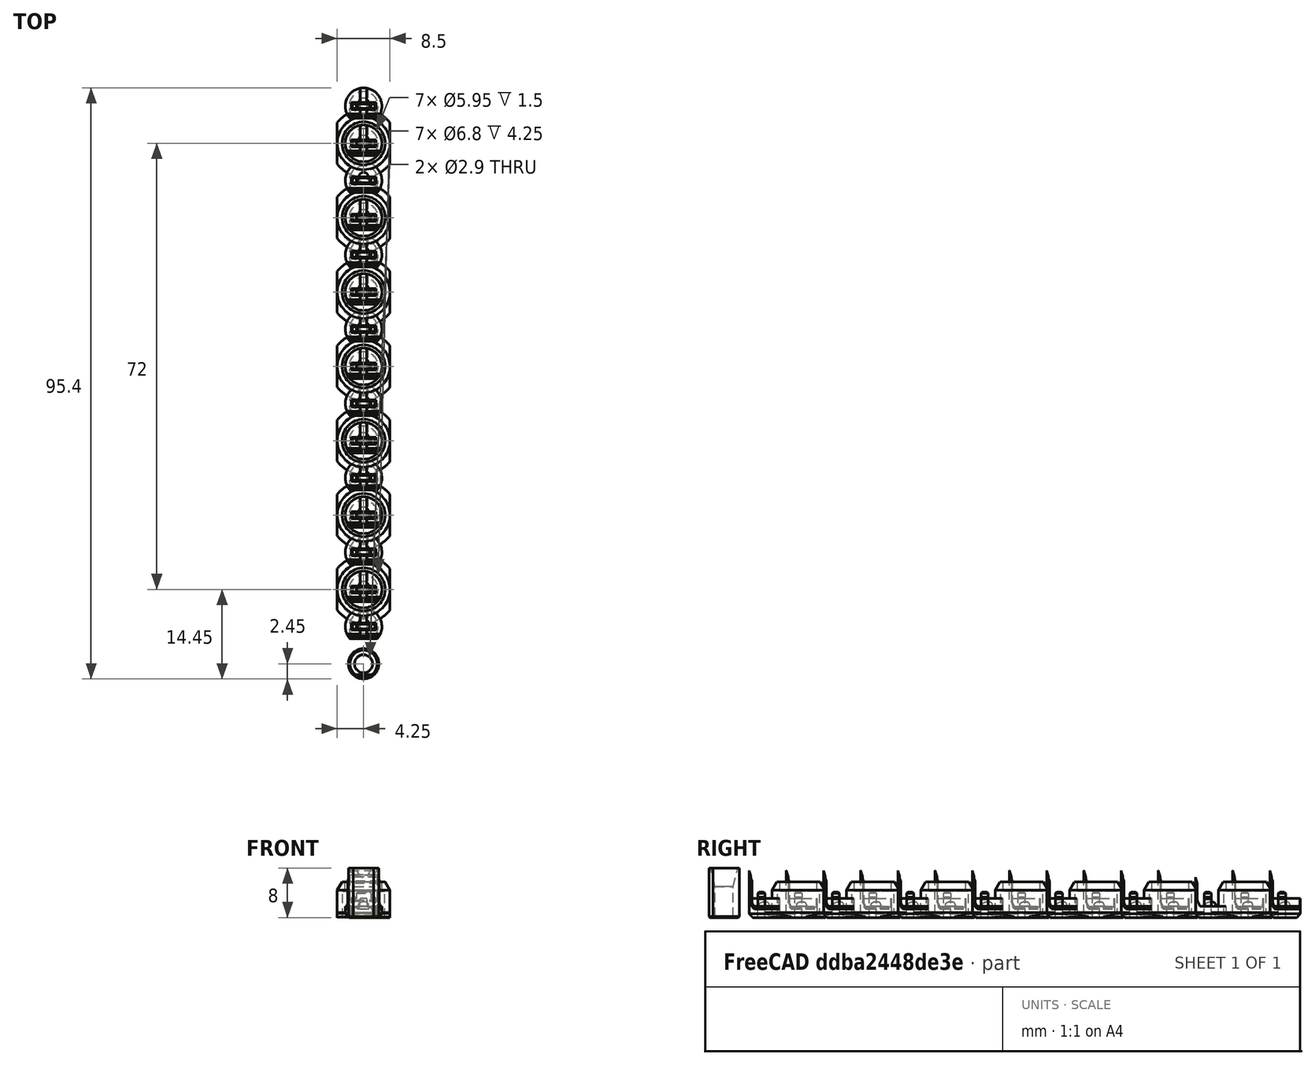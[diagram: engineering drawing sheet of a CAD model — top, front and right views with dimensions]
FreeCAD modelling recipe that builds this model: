
FCSTD DOCUMENT  (FreeCAD 0.21R33771 (Git))
Label: universal_insert
License: All rights reserved
LicenseURL: http://en.wikipedia.org/wiki/All_rights_reserved
objects: PartDesign::Body×90, PartDesign::FeatureBase×82, Sketcher::SketchObject×19, PartDesign::Pad×9, PartDesign::Pocket×7, PartDesign::Chamfer×7, App::Part×6, PartDesign::Revolution×3, PartDesign::Fillet×2, PartDesign::Draft×1
note: 249 computed .brp shape members not serialized (recipe doc carries the construction recipe); baked Part::Feature solids carry a one-line shape summary decoded from their .brp

FEATURE [Sketcher::SketchObject] Sketch
  FullyConstrained = false
  MapMode = 5
  Support = -> [XY_Plane]
  sketch-geometry (2):
    g0: ArcOfCircle CenterX=0 CenterY=0 CenterZ=0 NormalX=0 NormalY=0 NormalZ=1 AngleXU=0 Radius=2.95 StartAngle=5.55407 EndAngle=10.1539
    g1: LineSegment StartX=-2.2 StartY=-1.96532 StartZ=0 EndX=2.2 EndY=-1.96532 EndZ=0
  constraints (6):
    c: Coincident(g0,g-1)
    c: Coincident(g1,g0)
    c: Coincident(g1,g0)
    c: Radius(g0) = 2.95
    c: DistanceX(g1,g1) = 4.4
    c: Horizontal(g1)
FEATURE [PartDesign::Pad] Pad  label="Riser"
  AllowMultiFace = false
  Direction = (1,1,1)
  Length = 1.6
  Length2 = 100
  Profile = -> Sketch
  Refine = true
  Type = 0
FEATURE [Sketcher::SketchObject] Sketch001
  ExternalGeometry = -> [Pad]
  FullyConstrained = true
  MapMode = 5
  Placement = pos=(0,0,1.6) rot=(0,0,1;0rad)
  Support = -> [Pad]
  sketch-geometry (4):
    g0: LineSegment StartX=-0.5 StartY=-1.96532 StartZ=0 EndX=-0.5 EndY=2.90732 EndZ=0
    g1: LineSegment StartX=0.5 StartY=2.90732 StartZ=0 EndX=0.5 EndY=-1.96532 EndZ=0
    g2: ArcOfCircle CenterX=0 CenterY=0 CenterZ=0 NormalX=0 NormalY=0 NormalZ=1 AngleXU=0 Radius=2.95 StartAngle=1.40048 EndAngle=1.74111
    g3: LineSegment StartX=-0.5 StartY=-1.96532 StartZ=0 EndX=0.5 EndY=-1.96532 EndZ=0
  constraints (12):
    c: PointOnObject(g0,g-4)
    c: PointOnObject(g0,g-3)
    c: Vertical(g0)
    c: PointOnObject(g1,g-4)
    c: Vertical(g1)
    c: Coincident(g2,g-1)
    c: Coincident(g2,g0)
    c: Coincident(g2,g1)
    c: Equal(g1,g0)
    c: Coincident(g3,g0)
    c: Coincident(g3,g1)
    c: DistanceX(g3,g3) = 1
FEATURE [Sketcher::SketchObject] Sketch002
  ExternalGeometry = -> [Pad]
  FullyConstrained = false
  MapMode = 5
  Placement = pos=(0,0,1.6) rot=(0,0,1;0rad)
  Support = -> [Pad]
  sketch-geometry (4):
    g0: LineSegment StartX=-2.2 StartY=-1.96532 StartZ=0 EndX=2.2 EndY=-1.96532 EndZ=0
    g1: LineSegment StartX=-2.68803 StartY=-1.21532 StartZ=0 EndX=2.68803 EndY=-1.21532 EndZ=0
    g2: ArcOfCircle CenterX=0 CenterY=0 CenterZ=0 NormalX=0 NormalY=0 NormalZ=1 AngleXU=0 Radius=2.95 StartAngle=3.56621 EndAngle=3.87071
    g3: ArcOfCircle CenterX=0 CenterY=0 CenterZ=0 NormalX=0 NormalY=0 NormalZ=1 AngleXU=0 Radius=2.95 StartAngle=5.55407 EndAngle=5.85857
  constraints (10):
    c: Horizontal(g1)
    c: Coincident(g2,g-1)
    c: Coincident(g2,g0)
    c: Coincident(g2,g1)
    c: Coincident(g3,g2)
    c: Coincident(g3,g1)
    c: Coincident(g3,g0)
    c: DistanceY(g0,g1) = 0.75
    c: Coincident(g0,g-3)
    c: Coincident(g0,g-3)
FEATURE [PartDesign::Pad] Pad001
  AllowMultiFace = false
  BaseFeature = -> Pad
  Direction = (1,1,1)
  Length = 6
  Length2 = 100
  Profile = -> Sketch002
  Refine = true
  Type = 0
FEATURE [Sketcher::SketchObject] Sketch003
  ExternalGeometry = -> [Pad001]
  FullyConstrained = true
  MapMode = 5
  Placement = pos=(0,0,0) rot=(0.57735,0.57735,0.57735;2.0944rad)
  Support = -> [YZ_Plane]
  sketch-geometry (5):
    g0: LineSegment StartX=-1.21532 StartY=1.6 StartZ=0 EndX=-1.21532 EndY=7.6 EndZ=0
    g1: LineSegment StartX=-1.21532 StartY=1.6 StartZ=0 EndX=-1.66532 EndY=2.6 EndZ=0
    g2: LineSegment StartX=-1.96532 StartY=7.6 StartZ=0 EndX=-1.21532 EndY=7.6 EndZ=0
    g3: LineSegment StartX=-1.66532 StartY=2.6 StartZ=0 EndX=-1.66532 EndY=6.6 EndZ=0
    g4: LineSegment StartX=-1.66532 StartY=6.6 StartZ=0 EndX=-1.96532 EndY=7.6 EndZ=0
  constraints (13):
    c: Coincident(g0,g-3)
    c: Coincident(g0,g-3)
    c: Coincident(g1,g0)
    c: Horizontal(g2)
    c: Coincident(g2,g0)
    c: DistanceY(g0,g1) = 1
    c: Coincident(g3,g1)
    c: Vertical(g3)
    c: Coincident(g4,g3)
    c: Coincident(g4,g2)
    c: DistanceX(g2,g2) = 0.75
    c: DistanceY(g3,g0) = 1
    c: DistanceX(g2,g3) = 0.3
FEATURE [PartDesign::Pocket] Pocket
  AllowMultiFace = false
  BaseFeature = -> Pad001
  Direction = (1,1,1)
  Length = 5
  Length2 = 100
  Midplane = true
  Profile = -> Sketch003
  Refine = true
  Type = 1
FEATURE [PartDesign::Pad] Pad002
  AllowMultiFace = false
  BaseFeature = -> Pocket
  Direction = (1,1,1)
  Length = 1.5
  Length2 = 100
  Profile = -> Sketch001
  Refine = true
  Type = 0
FEATURE [PartDesign::Draft] Draft
  Angle = 6
  Base = -> Pad002 [Face9,Face11]
  BaseFeature = -> Pad002
  NeutralPlane = -> Pad002 [Face10]
  Reversed = true
  SupportTransform = false
FEATURE [PartDesign::Chamfer] Chamfer
  Angle = 45
  Base = -> Draft [Edge1,Edge2]
  BaseFeature = -> Draft
  ChamferType = 0
  FlipDirection = false
  Size = 0.6
  Size2 = 1
  SupportTransform = false
  UseAllEdges = false
FEATURE [PartDesign::Body] Body  label="Potentiometer"
  Group = -> [Sketch,Pad,Sketch001,Sketch002,Pad001,Sketch003,Pocket,Pad002,Draft,Chamfer]
  Origin = -> Origin
  Tip = -> Chamfer
FEATURE [Sketcher::SketchObject] Sketch004
  FullyConstrained = false
  MapMode = 5
  Support = -> [XY_Plane001]
  sketch-geometry (2):
    g0: ArcOfCircle CenterX=0 CenterY=0 CenterZ=0 NormalX=0 NormalY=0 NormalZ=1 AngleXU=0 Radius=2.95 StartAngle=5.55407 EndAngle=10.1539
    g1: LineSegment StartX=-2.2 StartY=-1.96532 StartZ=0 EndX=2.2 EndY=-1.96532 EndZ=0
  constraints (6):
    c: Coincident(g0,g-1)
    c: Coincident(g1,g0)
    c: Coincident(g1,g0)
    c: Radius(g0) = 2.95
    c: DistanceX(g1,g1) = 4.4
    c: Horizontal(g1)
FEATURE [PartDesign::Pad] Pad003  label="Riser001"
  AllowMultiFace = false
  Direction = (1,1,1)
  Length = 6.5
  Length2 = 100
  Profile = -> Sketch004
  Refine = true
  Type = 0
FEATURE [Sketcher::SketchObject] Sketch008
  FullyConstrained = true
  MapMode = 5
  Support = -> [XY_Plane002]
  sketch-geometry (7):
    g0: LineSegment StartX=-2 StartY=0.575 StartZ=0 EndX=2 EndY=0.575 EndZ=0
    g1: LineSegment StartX=2 StartY=0.575 StartZ=0 EndX=2 EndY=-0.575 EndZ=0
    g2: LineSegment StartX=2 StartY=-0.575 StartZ=0 EndX=-2 EndY=-0.575 EndZ=0
    g3: LineSegment StartX=-2 StartY=-0.575 StartZ=0 EndX=-2 EndY=0.575 EndZ=0
    g4: LineSegment StartX=-2 StartY=0.575 StartZ=0 EndX=0 EndY=0 EndZ=0
    g5: LineSegment StartX=0 StartY=0 StartZ=0 EndX=2 EndY=0.575 EndZ=0
    g6: LineSegment StartX=0 StartY=0 StartZ=0 EndX=-2 EndY=-0.575 EndZ=0
  constraints (18):
    c: Coincident(g0,g1)
    c: Coincident(g1,g2)
    c: Coincident(g2,g3)
    c: Coincident(g3,g0)
    c: Horizontal(g0)
    c: Horizontal(g2)
    c: Vertical(g1)
    c: Vertical(g3)
    c: Coincident(g4,g0)
    c: Coincident(g4,g-1)
    c: Coincident(g5,g-1)
    c: Coincident(g5,g0)
    c: Coincident(g6,g-1)
    c: Coincident(g6,g2)
    c: Equal(g6,g4)
    c: Equal(g4,g5)
    c: DistanceX(g0,g0) = 4
    c: DistanceY(g1,g1) = 1.15
FEATURE [PartDesign::Pad] Pad005  label="Riser002"
  AllowMultiFace = false
  Direction = (1,1,1)
  Length = 4.1
  Length2 = 100
  Profile = -> Sketch008
  Refine = true
  Type = 0
FEATURE [Sketcher::SketchObject] Sketch009
  ExternalGeometry = -> [Pad005]
  FullyConstrained = true
  MapMode = 5
  Placement = pos=(0,0.575,0) rot=(0,0.707107,0.707107;3.14159rad)
  Support = -> [Pad005]
  sketch-geometry (8):
    g0: LineSegment StartX=-2 StartY=4.1 StartZ=0 EndX=-1.175 EndY=4.1 EndZ=0
    g1: LineSegment StartX=-1.175 StartY=4.1 StartZ=0 EndX=-1.175 EndY=3.25 EndZ=0
    g2: LineSegment StartX=-1.175 StartY=3.25 StartZ=0 EndX=-2 EndY=3.25 EndZ=0
    g3: LineSegment StartX=-2 StartY=3.25 StartZ=0 EndX=-2 EndY=4.1 EndZ=0
    g4: LineSegment StartX=2 StartY=4.1 StartZ=0 EndX=1.175 EndY=4.1 EndZ=0
    g5: LineSegment StartX=1.175 StartY=4.1 StartZ=0 EndX=1.175 EndY=3.25 EndZ=0
    g6: LineSegment StartX=1.175 StartY=3.25 StartZ=0 EndX=2 EndY=3.25 EndZ=0
    g7: LineSegment StartX=2 StartY=3.25 StartZ=0 EndX=2 EndY=4.1 EndZ=0
  constraints (22):
    c: Coincident(g0,g1)
    c: Coincident(g1,g2)
    c: Coincident(g2,g3)
    c: Coincident(g3,g0)
    c: Horizontal(g0)
    c: Horizontal(g2)
    c: Vertical(g1)
    c: Vertical(g3)
    c: Coincident(g0,g-4)
    c: Coincident(g4,g5)
    c: Coincident(g5,g6)
    c: Coincident(g6,g7)
    c: Coincident(g7,g4)
    c: Horizontal(g4)
    c: Horizontal(g6)
    c: Vertical(g5)
    c: Vertical(g7)
    c: Coincident(g4,g-5)
    c: Equal(g4,g0)
    c: Equal(g1,g5)
    c: DistanceX(g0,g4) = 2.35
    c: DistanceY(g1,g1) = 0.85
FEATURE [PartDesign::Pocket] Pocket002
  AllowMultiFace = false
  BaseFeature = -> Pad005
  Direction = (1,1,1)
  Length = 5
  Length2 = 100
  Profile = -> Sketch009
  Refine = true
  Type = 0
FEATURE [Sketcher::SketchObject] Sketch010
  FullyConstrained = false
  MapMode = 5
  Placement = pos=(0,0,0) rot=(1,0,0;1.5708rad)
  Support = -> [XZ_Plane003]
  sketch-geometry (5):
    g0: LineSegment StartX=-1.45 StartY=0 StartZ=0 EndX=-1.45 EndY=5 EndZ=0
    g1: LineSegment StartX=-1.45 StartY=0 StartZ=0 EndX=-2.45 EndY=0 EndZ=0
    g2: LineSegment StartX=-2.45 StartY=0 StartZ=0 EndX=-2.45 EndY=8 EndZ=0
    g3: LineSegment StartX=-1.45 StartY=5 StartZ=0 EndX=-2.2 EndY=8 EndZ=0
    g4: LineSegment StartX=-2.45 StartY=8 StartZ=0 EndX=-2.2 EndY=8 EndZ=0
  constraints (15):
    c: PointOnObject(g0,g-1)
    c: Coincident(g1,g0)
    c: Horizontal(g1)
    c: Coincident(g2,g1)
    c: Vertical(g2)
    c: DistanceX(g0,g-1) = 1.45
    c: Vertical(g0)
    c: Coincident(g3,g0)
    c: DistanceX(g1,g1) = 1
    c: Coincident(g4,g2)
    c: Coincident(g4,g3)
    c: Horizontal(g4)
    c: DistanceX(g4,g4) = 0.25
    c: DistanceY(g2,g2) = 8
    c: DistanceY(g0,g0) = 5
FEATURE [PartDesign::Revolution] Revolution
  AllowMultiFace = false
  Angle = 360
  Axis = (0,-2e-16,1)
  Base = (0,0,0)
  Placement = pos=(0,0,0) rot=(1,0,0;1.5708rad)
  Profile = -> Sketch010
  ReferenceAxis = -> Sketch010 [V_Axis]
  Refine = true
FEATURE [Sketcher::SketchObject] Sketch011
  FullyConstrained = false
  MapMode = 5
  Placement = pos=(0,0,0) rot=(1,0,0;1.5708rad)
  Support = -> [XZ_Plane004]
  sketch-geometry (5):
    g0: LineSegment StartX=-1.45 StartY=0 StartZ=0 EndX=-1.45 EndY=5 EndZ=0
    g1: LineSegment StartX=-1.45 StartY=0 StartZ=0 EndX=-2.45 EndY=0 EndZ=0
    g2: LineSegment StartX=-2.45 StartY=0 StartZ=0 EndX=-2.45 EndY=8 EndZ=0
    g3: LineSegment StartX=-1.45 StartY=5 StartZ=0 EndX=-2.2 EndY=8 EndZ=0
    g4: LineSegment StartX=-2.45 StartY=8 StartZ=0 EndX=-2.2 EndY=8 EndZ=0
  constraints (15):
    c: PointOnObject(g0,g-1)
    c: Coincident(g1,g0)
    c: Horizontal(g1)
    c: Coincident(g2,g1)
    c: Vertical(g2)
    c: DistanceX(g0,g-1) = 1.45
    c: Vertical(g0)
    c: Coincident(g3,g0)
    c: DistanceX(g1,g1) = 1
    c: Coincident(g4,g2)
    c: Coincident(g4,g3)
    c: Horizontal(g4)
    c: DistanceX(g4,g4) = 0.25
    c: DistanceY(g2,g2) = 8
    c: DistanceY(g0,g0) = 5
FEATURE [PartDesign::Revolution] Revolution001
  AllowMultiFace = false
  Angle = 360
  Axis = (0,-2e-16,1)
  Base = (0,0,0)
  Placement = pos=(0,0,0) rot=(1,0,0;1.5708rad)
  Profile = -> Sketch011
  ReferenceAxis = -> Sketch011 [V_Axis]
  Refine = true
FEATURE [Sketcher::SketchObject] Sketch012
  FullyConstrained = false
  MapMode = 5
  Placement = pos=(0,0,0) rot=(1,0,0;3.14159rad)
  Support = -> [Revolution001]
  sketch-geometry (4):
    g0: LineSegment StartX=-2.03437 StartY=2.61565 StartZ=0 EndX=2.45071 EndY=2.61565 EndZ=0
    g1: LineSegment StartX=2.45071 StartY=2.61565 StartZ=0 EndX=2.45071 EndY=1.8 EndZ=0
    g2: LineSegment StartX=2.45071 StartY=1.8 StartZ=0 EndX=-2.03437 EndY=1.8 EndZ=0
    g3: LineSegment StartX=-2.03437 StartY=1.8 StartZ=0 EndX=-2.03437 EndY=2.61565 EndZ=0
  constraints (9):
    c: Coincident(g0,g1)
    c: Coincident(g1,g2)
    c: Coincident(g2,g3)
    c: Coincident(g3,g0)
    c: Horizontal(g0)
    c: Horizontal(g2)
    c: Vertical(g1)
    c: Vertical(g3)
    c: DistanceY(g-1,g2) = 1.8
FEATURE [PartDesign::Pocket] Pocket003
  AllowMultiFace = false
  BaseFeature = -> Revolution001
  Direction = (1,1,1)
  Length = 5
  Length2 = 100
  Placement = pos=(0,0,0) rot=(1,0,0;1.5708rad)
  Profile = -> Sketch012
  Refine = true
  Type = 1
FEATURE [PartDesign::Chamfer] Chamfer002
  Angle = 45
  Base = -> Revolution [Face5]
  BaseFeature = -> Revolution
  ChamferType = 0
  FlipDirection = false
  Placement = pos=(0,0,0) rot=(1,0,0;1.5708rad)
  Size = 0.15
  Size2 = 1
  SupportTransform = false
  UseAllEdges = false
FEATURE [PartDesign::Body] Body003  label="Light_Standard"
  Group = -> [Sketch010,Revolution,Chamfer002]
  Origin = -> Origin003
  Tip = -> Chamfer002
FEATURE [PartDesign::Chamfer] Chamfer003
  Angle = 45
  Base = -> Pocket003 [Face2]
  BaseFeature = -> Pocket003
  ChamferType = 0
  FlipDirection = false
  Placement = pos=(0,0,0) rot=(1,0,0;1.5708rad)
  Size = 0.15
  Size2 = 1
  SupportTransform = false
  UseAllEdges = false
FEATURE [PartDesign::Body] Body004  label="Light_Cut"
  Group = -> [Sketch011,Revolution001,Sketch012,Pocket003,Chamfer003]
  Origin = -> Origin004
  Tip = -> Chamfer003
FEATURE [PartDesign::FeatureBase] Clone
  BaseFeature = -> Body
FEATURE [PartDesign::Body] Body005
  BaseFeature = -> Body
  Group = -> [Clone]
  Origin = -> Origin006
  Placement = pos=(0,6,0) rot=(0,0,1;0rad)
  Tip = -> Clone
FEATURE [PartDesign::FeatureBase] Clone001
  BaseFeature = -> Body
FEATURE [PartDesign::Body] Body006
  BaseFeature = -> Body
  Group = -> [Clone001]
  Origin = -> Origin007
  Placement = pos=(0,12,0) rot=(0,0,1;0rad)
  Tip = -> Clone001
FEATURE [PartDesign::FeatureBase] Clone002
  BaseFeature = -> Body
FEATURE [PartDesign::Body] Body007
  BaseFeature = -> Body
  Group = -> [Clone002]
  Origin = -> Origin008
  Placement = pos=(0,18,0) rot=(0,0,1;0rad)
  Tip = -> Clone002
FEATURE [PartDesign::FeatureBase] Clone003
  BaseFeature = -> Body
FEATURE [PartDesign::Body] Body008
  BaseFeature = -> Body
  Group = -> [Clone003]
  Origin = -> Origin009
  Placement = pos=(0,24,0) rot=(0,0,1;0rad)
  Tip = -> Clone003
FEATURE [PartDesign::FeatureBase] Clone004
  BaseFeature = -> Body
FEATURE [PartDesign::Body] Body009
  BaseFeature = -> Body
  Group = -> [Clone004]
  Origin = -> Origin010
  Placement = pos=(0,30,0) rot=(0,0,1;0rad)
  Tip = -> Clone004
FEATURE [PartDesign::FeatureBase] Clone005
  BaseFeature = -> Body
FEATURE [PartDesign::Body] Body010
  BaseFeature = -> Body
  Group = -> [Clone005]
  Origin = -> Origin011
  Placement = pos=(0,36,0) rot=(0,0,1;0rad)
  Tip = -> Clone005
FEATURE [PartDesign::FeatureBase] Clone006
  BaseFeature = -> Body
FEATURE [PartDesign::Body] Body011
  BaseFeature = -> Body
  Group = -> [Clone006]
  Origin = -> Origin012
  Placement = pos=(0,42,0) rot=(0,0,1;0rad)
  Tip = -> Clone006
FEATURE [PartDesign::FeatureBase] Clone007
  BaseFeature = -> Body
FEATURE [PartDesign::Body] Body012
  BaseFeature = -> Body
  Group = -> [Clone007]
  Origin = -> Origin013
  Placement = pos=(0,48,0) rot=(0,0,1;0rad)
  Tip = -> Clone007
FEATURE [PartDesign::FeatureBase] Clone008
  BaseFeature = -> Body
FEATURE [PartDesign::Body] Body013
  BaseFeature = -> Body
  Group = -> [Clone008]
  Origin = -> Origin014
  Placement = pos=(0,54,0) rot=(0,0,1;0rad)
  Tip = -> Clone008
FEATURE [PartDesign::FeatureBase] Clone009
  BaseFeature = -> Body
FEATURE [PartDesign::Body] Body014
  BaseFeature = -> Body
  Group = -> [Clone009]
  Origin = -> Origin015
  Placement = pos=(0,60,0) rot=(0,0,1;0rad)
  Tip = -> Clone009
FEATURE [PartDesign::FeatureBase] Clone010
  BaseFeature = -> Body
FEATURE [PartDesign::Body] Body015
  BaseFeature = -> Body
  Group = -> [Clone010]
  Origin = -> Origin016
  Placement = pos=(0,66,0) rot=(0,0,1;0rad)
  Tip = -> Clone010
FEATURE [PartDesign::FeatureBase] Clone011
  BaseFeature = -> Body
FEATURE [PartDesign::Body] Body016
  BaseFeature = -> Body
  Group = -> [Clone011]
  Origin = -> Origin017
  Placement = pos=(0,72,0) rot=(0,0,1;0rad)
  Tip = -> Clone011
FEATURE [PartDesign::FeatureBase] Clone012
  BaseFeature = -> Body
FEATURE [PartDesign::Body] Body017
  BaseFeature = -> Body
  Group = -> [Clone012]
  Origin = -> Origin018
  Placement = pos=(0,78,0) rot=(0,0,1;0rad)
  Tip = -> Clone012
FEATURE [PartDesign::FeatureBase] Clone013
  BaseFeature = -> Body017
FEATURE [PartDesign::Body] Body018
  BaseFeature = -> Body017
  Group = -> [Clone013]
  Origin = -> Origin019
  Placement = pos=(0,84,0) rot=(0,0,1;0rad)
  Tip = -> Clone013
FEATURE [PartDesign::FeatureBase] Clone014
  BaseFeature = -> Body017
FEATURE [PartDesign::Body] Body019
  BaseFeature = -> Body017
  Group = -> [Clone014]
  Origin = -> Origin020
  Placement = pos=(0,90,0) rot=(0,0,1;0rad)
  Tip = -> Clone014
FEATURE [App::Part] Part  label="P"
  Group = -> [Body,Body005,Body006,Body007,Body008,Body009,Body010,Body011,Body012,Body013,Body014,Body015,Body016,Body017,Body018,Body019]
  Origin = -> Origin005
FEATURE [Sketcher::SketchObject] Sketch014
  FullyConstrained = true
  MapMode = 5
  Placement = pos=(0,0,0) rot=(0.57735,0.57735,0.57735;2.0944rad)
  Support = -> [YZ_Plane001]
  expr: Constraints[17] = 1.5 + 0.3
  sketch-geometry (6):
    g0: LineSegment StartX=-1.97 StartY=6.5 StartZ=0 EndX=-1.67 EndY=5.5 EndZ=0
    g1: LineSegment StartX=-1.67 StartY=5.5 StartZ=0 EndX=-1.67 EndY=2.8 EndZ=0
    g2: LineSegment StartX=-1.67 StartY=2.8 StartZ=0 EndX=-1.22 EndY=1.8 EndZ=0
    g3: LineSegment StartX=-1.22 StartY=1.8 StartZ=0 EndX=4 EndY=1.8 EndZ=0
    g4: LineSegment StartX=4 StartY=1.8 StartZ=0 EndX=4 EndY=6.5 EndZ=0
    g5: LineSegment StartX=4 StartY=6.5 StartZ=0 EndX=-1.97 EndY=6.5 EndZ=0
  constraints (18):
    c: Coincident(g0,g1)
    c: Vertical(g1)
    c: Coincident(g1,g2)
    c: Coincident(g2,g3)
    c: Horizontal(g3)
    c: Coincident(g3,g4)
    c: Vertical(g4)
    c: Coincident(g4,g5)
    c: Coincident(g5,g0)
    c: Horizontal(g5)
    c: DistanceX(g0,g-1) = 1.97
    c: DistanceY(g-1,g0) = 6.5
    c: DistanceX(g0,g0) = 0.3
    c: DistanceY(g0,g0) = 1
    c: DistanceY(g2,g2) = 1
    c: DistanceX(g2,g2) = 0.45
    c: DistanceX(g-1,g3) = 4
    c: DistanceY(g-1,g3) = 1.8
FEATURE [PartDesign::Pocket] Pocket004
  BaseFeature = -> Pad003
  Direction = (1,1,1)
  Length = 5
  Length2 = 100
  Midplane = true
  Profile = -> Sketch014
  Type = 1
FEATURE [Sketcher::SketchObject] Sketch013
  FullyConstrained = true
  MapMode = 5
  Placement = pos=(-5e-16,4e-16,1.8) rot=(0,0,1;0rad)
  Support = -> [Pocket004]
  sketch-geometry (1):
    g0: Circle CenterX=0 CenterY=0.5 CenterZ=0 NormalX=0 NormalY=0 NormalZ=1 AngleXU=0 Radius=0.8
  constraints (3):
    c: PointOnObject(g0,g-2)
    c: DistanceY(g-1,g0) = 0.5
    c: Diameter(g0) = 1.6
FEATURE [PartDesign::Pad] Pad006
  BaseFeature = -> Pocket004
  Direction = (1,1,1)
  Length = 0.7
  Length2 = 100
  Profile = -> Sketch013
  Type = 0
FEATURE [PartDesign::Fillet] Fillet
  Base = -> Pad006 [Edge18]
  BaseFeature = -> Pad006
  Radius = 0.5
  SupportTransform = false
  UseAllEdges = false
FEATURE [PartDesign::Chamfer] Chamfer004
  Angle = 45
  Base = -> Fillet [Face7]
  BaseFeature = -> Fillet
  ChamferType = 0
  FlipDirection = false
  Size = 0.6
  Size2 = 1
  SupportTransform = false
  UseAllEdges = false
FEATURE [PartDesign::Body] Body001  label="Encoder"
  Group = -> [Sketch004,Pad003,Sketch013,Sketch014,Pocket004,Pad006,Fillet,Chamfer004]
  Origin = -> Origin001
  Tip = -> Chamfer004
FEATURE [PartDesign::FeatureBase] Clone015
  BaseFeature = -> Body001
FEATURE [PartDesign::Body] Body020
  BaseFeature = -> Body001
  Group = -> [Clone015]
  Origin = -> Origin022
  Placement = pos=(0,6,0) rot=(0,0,1;0rad)
  Tip = -> Clone015
FEATURE [PartDesign::FeatureBase] Clone016
  BaseFeature = -> Body001
FEATURE [PartDesign::Body] Body021
  BaseFeature = -> Body001
  Group = -> [Clone016]
  Origin = -> Origin023
  Placement = pos=(0,12,0) rot=(0,0,1;0rad)
  Tip = -> Clone016
FEATURE [PartDesign::FeatureBase] Clone017
  BaseFeature = -> Body001
FEATURE [PartDesign::Body] Body022
  BaseFeature = -> Body001
  Group = -> [Clone017]
  Origin = -> Origin024
  Placement = pos=(0,18,0) rot=(0,0,1;0rad)
  Tip = -> Clone017
FEATURE [PartDesign::FeatureBase] Clone018
  BaseFeature = -> Body001
FEATURE [PartDesign::Body] Body023
  BaseFeature = -> Body001
  Group = -> [Clone018]
  Origin = -> Origin025
  Placement = pos=(0,24,0) rot=(0,0,1;0rad)
  Tip = -> Clone018
FEATURE [PartDesign::FeatureBase] Clone019
  BaseFeature = -> Body001
FEATURE [PartDesign::Body] Body024
  BaseFeature = -> Body001
  Group = -> [Clone019]
  Origin = -> Origin026
  Placement = pos=(0,30,0) rot=(0,0,1;0rad)
  Tip = -> Clone019
FEATURE [PartDesign::FeatureBase] Clone020
  BaseFeature = -> Body001
FEATURE [PartDesign::Body] Body025
  BaseFeature = -> Body001
  Group = -> [Clone020]
  Origin = -> Origin027
  Placement = pos=(0,36,0) rot=(0,0,1;0rad)
  Tip = -> Clone020
FEATURE [PartDesign::FeatureBase] Clone021
  BaseFeature = -> Body001
FEATURE [PartDesign::Body] Body026
  BaseFeature = -> Body001
  Group = -> [Clone021]
  Origin = -> Origin028
  Placement = pos=(0,42,0) rot=(0,0,1;0rad)
  Tip = -> Clone021
FEATURE [PartDesign::FeatureBase] Clone022
  BaseFeature = -> Body001
FEATURE [PartDesign::Body] Body027
  BaseFeature = -> Body001
  Group = -> [Clone022]
  Origin = -> Origin029
  Placement = pos=(0,48,0) rot=(0,0,1;0rad)
  Tip = -> Clone022
FEATURE [PartDesign::FeatureBase] Clone023
  BaseFeature = -> Body001
FEATURE [PartDesign::Body] Body028
  BaseFeature = -> Body001
  Group = -> [Clone023]
  Origin = -> Origin030
  Placement = pos=(0,54,0) rot=(0,0,1;0rad)
  Tip = -> Clone023
FEATURE [PartDesign::FeatureBase] Clone024
  BaseFeature = -> Body001
FEATURE [PartDesign::Body] Body029
  BaseFeature = -> Body001
  Group = -> [Clone024]
  Origin = -> Origin031
  Placement = pos=(0,60,0) rot=(0,0,1;0rad)
  Tip = -> Clone024
FEATURE [PartDesign::FeatureBase] Clone025
  BaseFeature = -> Body001
FEATURE [PartDesign::Body] Body030
  BaseFeature = -> Body001
  Group = -> [Clone025]
  Origin = -> Origin032
  Placement = pos=(0,66,0) rot=(0,0,1;0rad)
  Tip = -> Clone025
FEATURE [PartDesign::FeatureBase] Clone026
  BaseFeature = -> Body001
FEATURE [PartDesign::Body] Body031
  BaseFeature = -> Body001
  Group = -> [Clone026]
  Origin = -> Origin033
  Placement = pos=(0,72,0) rot=(0,0,1;0rad)
  Tip = -> Clone026
FEATURE [PartDesign::FeatureBase] Clone027
  BaseFeature = -> Body001
FEATURE [PartDesign::Body] Body032
  BaseFeature = -> Body001
  Group = -> [Clone027]
  Origin = -> Origin034
  Placement = pos=(0,78,0) rot=(0,0,1;0rad)
  Tip = -> Clone027
FEATURE [PartDesign::FeatureBase] Clone028
  BaseFeature = -> Body001
FEATURE [PartDesign::Body] Body033
  BaseFeature = -> Body001
  Group = -> [Clone028]
  Origin = -> Origin035
  Placement = pos=(0,84,0) rot=(0,0,1;0rad)
  Tip = -> Clone028
FEATURE [PartDesign::FeatureBase] Clone029
  BaseFeature = -> Body001
FEATURE [PartDesign::Body] Body034
  BaseFeature = -> Body001
  Group = -> [Clone029]
  Origin = -> Origin036
  Placement = pos=(0,90,0) rot=(0,0,1;0rad)
  Tip = -> Clone029
FEATURE [App::Part] Part002  label="E"
  Group = -> [Body001,Body020,Body021,Body022,Body023,Body024,Body025,Body026,Body027,Body028,Body029,Body030,Body031,Body032,Body033,Body034]
  Origin = -> Origin037
FEATURE [PartDesign::Chamfer] Chamfer005
  Angle = 45
  Base = -> Pocket002 [Edge5,Edge19,Edge3,Edge7,Edge23,Edge14,Edge13,Edge22,Edge17,Edge18]
  BaseFeature = -> Pocket002
  ChamferType = 0
  FlipDirection = false
  Size = 0.2
  Size2 = 1
  SupportTransform = false
  UseAllEdges = false
FEATURE [PartDesign::Body] Body002  label="Fader"
  Group = -> [Sketch008,Pad005,Sketch009,Pocket002,Chamfer005]
  Origin = -> Origin002
  Tip = -> Chamfer005
FEATURE [PartDesign::FeatureBase] Clone030
  BaseFeature = -> Body002
FEATURE [PartDesign::Body] Body035
  BaseFeature = -> Body002
  Group = -> [Clone030]
  Origin = -> Origin038
  Placement = pos=(0,6,0) rot=(0,0,1;0rad)
  Tip = -> Clone030
FEATURE [PartDesign::FeatureBase] Clone031
  BaseFeature = -> Body002
FEATURE [PartDesign::Body] Body036
  BaseFeature = -> Body002
  Group = -> [Clone031]
  Origin = -> Origin039
  Placement = pos=(0,12,0) rot=(0,0,1;0rad)
  Tip = -> Clone031
FEATURE [PartDesign::FeatureBase] Clone032
  BaseFeature = -> Body002
FEATURE [PartDesign::Body] Body037
  BaseFeature = -> Body002
  Group = -> [Clone032]
  Origin = -> Origin040
  Placement = pos=(0,18,0) rot=(0,0,1;0rad)
  Tip = -> Clone032
FEATURE [PartDesign::FeatureBase] Clone033
  BaseFeature = -> Body002
FEATURE [PartDesign::Body] Body038
  BaseFeature = -> Body002
  Group = -> [Clone033]
  Origin = -> Origin041
  Placement = pos=(0,24,0) rot=(0,0,1;0rad)
  Tip = -> Clone033
FEATURE [PartDesign::FeatureBase] Clone034
  BaseFeature = -> Body002
FEATURE [PartDesign::Body] Body039
  BaseFeature = -> Body002
  Group = -> [Clone034]
  Origin = -> Origin042
  Placement = pos=(0,30,0) rot=(0,0,1;0rad)
  Tip = -> Clone034
FEATURE [PartDesign::FeatureBase] Clone035
  BaseFeature = -> Body002
FEATURE [PartDesign::Body] Body040
  BaseFeature = -> Body002
  Group = -> [Clone035]
  Origin = -> Origin043
  Placement = pos=(0,36,0) rot=(0,0,1;0rad)
  Tip = -> Clone035
FEATURE [PartDesign::FeatureBase] Clone036
  BaseFeature = -> Body002
FEATURE [PartDesign::Body] Body041
  BaseFeature = -> Body002
  Group = -> [Clone036]
  Origin = -> Origin044
  Placement = pos=(0,42,0) rot=(0,0,1;0rad)
  Tip = -> Clone036
FEATURE [PartDesign::FeatureBase] Clone037
  BaseFeature = -> Body002
FEATURE [PartDesign::Body] Body042
  BaseFeature = -> Body002
  Group = -> [Clone037]
  Origin = -> Origin045
  Placement = pos=(0,48,0) rot=(0,0,1;0rad)
  Tip = -> Clone037
FEATURE [PartDesign::FeatureBase] Clone038
  BaseFeature = -> Body002
FEATURE [PartDesign::Body] Body043
  BaseFeature = -> Body002
  Group = -> [Clone038]
  Origin = -> Origin046
  Placement = pos=(0,54,0) rot=(0,0,1;0rad)
  Tip = -> Clone038
FEATURE [PartDesign::FeatureBase] Clone039
  BaseFeature = -> Body002
FEATURE [PartDesign::Body] Body044
  BaseFeature = -> Body002
  Group = -> [Clone039]
  Origin = -> Origin047
  Placement = pos=(0,60,0) rot=(0,0,1;0rad)
  Tip = -> Clone039
FEATURE [PartDesign::FeatureBase] Clone040
  BaseFeature = -> Body002
FEATURE [PartDesign::Body] Body045
  BaseFeature = -> Body002
  Group = -> [Clone040]
  Origin = -> Origin048
  Placement = pos=(0,66,0) rot=(0,0,1;0rad)
  Tip = -> Clone040
FEATURE [PartDesign::FeatureBase] Clone041
  BaseFeature = -> Body002
FEATURE [PartDesign::Body] Body046
  BaseFeature = -> Body002
  Group = -> [Clone041]
  Origin = -> Origin049
  Placement = pos=(0,72,0) rot=(0,0,1;0rad)
  Tip = -> Clone041
FEATURE [PartDesign::FeatureBase] Clone042
  BaseFeature = -> Body002
FEATURE [PartDesign::Body] Body047
  BaseFeature = -> Body002
  Group = -> [Clone042]
  Origin = -> Origin050
  Placement = pos=(0,78,0) rot=(0,0,1;0rad)
  Tip = -> Clone042
FEATURE [PartDesign::FeatureBase] Clone043
  BaseFeature = -> Body002
FEATURE [PartDesign::Body] Body048
  BaseFeature = -> Body002
  Group = -> [Clone043]
  Origin = -> Origin051
  Placement = pos=(0,84,0) rot=(0,0,1;0rad)
  Tip = -> Clone043
FEATURE [PartDesign::FeatureBase] Clone044
  BaseFeature = -> Body002
FEATURE [PartDesign::Body] Body049
  BaseFeature = -> Body002
  Group = -> [Clone044]
  Origin = -> Origin052
  Placement = pos=(0,90,0) rot=(0,0,1;0rad)
  Tip = -> Clone044
FEATURE [App::Part] Part001  label="F"
  Group = -> [Body002,Body035,Body036,Body037,Body038,Body039,Body040,Body041,Body042,Body043,Body044,Body045,Body046,Body047,Body048,Body049]
  Origin = -> Origin021
FEATURE [Sketcher::SketchObject] Sketch018
  FullyConstrained = true
  MapMode = 5
  Support = -> [XY_Plane053]
  sketch-geometry (2):
    g0: ArcOfCircle CenterX=0 CenterY=0 CenterZ=0 NormalX=0 NormalY=0 NormalZ=1 AngleXU=0 Radius=2.95 StartAngle=5.55407 EndAngle=10.1539
    g1: LineSegment StartX=-2.2 StartY=-1.96532 StartZ=0 EndX=2.2 EndY=-1.96532 EndZ=0
  constraints (6):
    c: Coincident(g0,g-1)
    c: Coincident(g1,g0)
    c: Coincident(g1,g0)
    c: Radius(g0) = 2.95
    c: DistanceX(g1,g1) = 4.4
    c: Horizontal(g1)
FEATURE [PartDesign::Pad] Pad007  label="Riser003"
  AllowMultiFace = false
  Direction = (0,0,1)
  Length = 6.9
  Length2 = 100
  Profile = -> Sketch018
  ReferenceAxis = -> Sketch018 [N_Axis]
  Refine = true
  Type = 0
FEATURE [Sketcher::SketchObject] Sketch019
  FullyConstrained = true
  MapMode = 5
  Placement = pos=(0,0,0) rot=(0.57735,0.57735,0.57735;2.0944rad)
  Support = -> [YZ_Plane053]
  sketch-geometry (6):
    g0: LineSegment StartX=-1.9 StartY=6.9 StartZ=0 EndX=-1.5 EndY=5.9 EndZ=0
    g1: LineSegment StartX=-1.5 StartY=5.9 StartZ=0 EndX=-1.5 EndY=1.75 EndZ=0
    g2: LineSegment StartX=-1.5 StartY=1.75 StartZ=0 EndX=-1.15 EndY=1.4 EndZ=0
    g3: LineSegment StartX=-1.15 StartY=1.4 StartZ=0 EndX=5 EndY=1.4 EndZ=0
    g4: LineSegment StartX=5 StartY=1.4 StartZ=0 EndX=5 EndY=6.9 EndZ=0
    g5: LineSegment StartX=5 StartY=6.9 StartZ=0 EndX=-1.9 EndY=6.9 EndZ=0
  constraints (18):
    c: Coincident(g0,g1)
    c: Vertical(g1)
    c: Coincident(g1,g2)
    c: Coincident(g2,g3)
    c: Horizontal(g3)
    c: Coincident(g3,g4)
    c: Vertical(g4)
    c: Coincident(g4,g5)
    c: Coincident(g5,g0)
    c: Horizontal(g5)
    c: DistanceY(g-1,g3) = 1.4
    c: DistanceX(g-1,g3) = 5
    c: Angle(g3,g2) = 2.35619
    c: DistanceX(g1,g2) = 0.35
    c: DistanceX(g1,g-1) = 1.5
    c: DistanceY(g-1,g0) = 6.9
    c: DistanceY(g0,g0) = 1
    c: DistanceX(g0,g-1) = 1.9
FEATURE [PartDesign::Pocket] Pocket005
  BaseFeature = -> Pad007
  Direction = (-1,2e-16,-3e-16)
  Length = 5
  Length2 = 100
  Midplane = true
  Profile = -> Sketch019
  Type = 1
FEATURE [Sketcher::SketchObject] Sketch020
  FullyConstrained = true
  MapMode = 5
  Placement = pos=(0,0,0) rot=(0.57735,0.57735,0.57735;2.0944rad)
  Support = -> [YZ_Plane070]
  sketch-geometry (11):
    g0: LineSegment StartX=3.4 StartY=0 StartZ=0 EndX=4.4 EndY=0 EndZ=0
    g1: LineSegment StartX=3.4 StartY=0 StartZ=0 EndX=3.4 EndY=4.25 EndZ=0
    g2: LineSegment StartX=3.4 StartY=4.25 StartZ=0 EndX=2.975 EndY=4.25 EndZ=0
    g3: LineSegment StartX=2.975 StartY=4.25 StartZ=0 EndX=2.975 EndY=5.75 EndZ=0
    g4: LineSegment StartX=5.4 StartY=0.8 StartZ=0 EndX=4.25 EndY=0.8 EndZ=0
    g5: LineSegment StartX=4.25 StartY=0.8 StartZ=0 EndX=4.25 EndY=4.40766 EndZ=0
    g6: LineSegment StartX=2.975 StartY=5.75 StartZ=0 EndX=3.475 EndY=5.75 EndZ=0
    g7: LineSegment StartX=3.475 StartY=5.75 StartZ=0 EndX=4.25 EndY=4.40766 EndZ=0
    g8: LineSegment StartX=5.4 StartY=0.8 StartZ=0 EndX=5.4 EndY=0.688675 EndZ=0
    g9: LineSegment StartX=5.4 StartY=0.688675 StartZ=0 EndX=4.4 EndY=0.111325 EndZ=0
    g10: LineSegment StartX=4.4 StartY=0.111325 StartZ=0 EndX=4.4 EndY=0 EndZ=0
  constraints (33):
    c: PointOnObject(g0,g-1)
    c: PointOnObject(g0,g-1)
    c: DistanceX(g-1,g0) = 3.4
    c: Coincident(g1,g0)
    c: Vertical(g1)
    c: DistanceY(g-1,g1) = 4.25
    c: Coincident(g1,g2)
    c: Coincident(g2,g3)
    c: Vertical(g3)
    c: Horizontal(g2)
    c: DistanceX(g-1,g2) = 2.975
    c: DistanceY(g3,g3) = 1.5
    c: Horizontal(g4)
    c: Coincident(g5,g4)
    c: Vertical(g5)
    c: DistanceX(g-1,g4) = 4.25
    c: Coincident(g6,g3)
    c: Coincident(g7,g6)
    c: Coincident(g7,g5)
    c: Horizontal(g6)
    c: Angle(g6,g7) = 2.0944
    c: DistanceX(g3,g6) = 0.5
    c: DistanceX(g0,g4) = 2
    c: DistanceY(g0,g4) = 0.8
    c: DistanceX(g0,g0) = 1
    c: Coincident(g4,g8)
    c: Vertical(g8)
    c: Coincident(g8,g9)
    c: Coincident(g9,g10)
    c: Coincident(g10,g0)
    c: Vertical(g10)
    c: Equal(g8,g10)
    c: Angle(g8,g9) = 2.0944
FEATURE [PartDesign::Revolution] Revolution002
  Angle = 360
  Axis = (-2e-16,3e-16,1)
  Base = (0,0,0)
  Placement = pos=(0,0,0) rot=(0.57735,0.57735,0.57735;2.0944rad)
  Profile = -> Sketch020
  ReferenceAxis = -> Sketch020 [V_Axis]
  Reversed = true
FEATURE [Sketcher::SketchObject] Sketch021
  FullyConstrained = false
  MapMode = 5
  Support = -> [XY_Plane070]
  sketch-geometry (13):
    g0: LineSegment StartX=-6.25 StartY=5.8823 StartZ=0 EndX=-4.25 EndY=5.8823 EndZ=0
    g1: LineSegment StartX=-4.25 StartY=5.8823 StartZ=0 EndX=-4.25 EndY=-5.8823 EndZ=0
    g2: LineSegment StartX=-4.25 StartY=-5.8823 StartZ=0 EndX=-6.25 EndY=-5.8823 EndZ=0
    g3: LineSegment StartX=-6.25 StartY=-5.8823 StartZ=0 EndX=-6.25 EndY=5.8823 EndZ=0
    g4: LineSegment StartX=6.25 StartY=5.8823 StartZ=0 EndX=4.25 EndY=5.8823 EndZ=0
    g5: LineSegment StartX=4.25 StartY=5.8823 StartZ=0 EndX=4.25 EndY=-5.8823 EndZ=0
    g6: LineSegment StartX=4.25 StartY=-5.8823 StartZ=0 EndX=6.25 EndY=-5.8823 EndZ=0
    g7: LineSegment StartX=6.25 StartY=-5.8823 StartZ=0 EndX=6.25 EndY=5.8823 EndZ=0
    g8: LineSegment StartX=-4.25 StartY=5.8823 StartZ=0 EndX=0 EndY=0 EndZ=0
    g9: LineSegment StartX=0 StartY=0 StartZ=0 EndX=4.25 EndY=5.8823 EndZ=0
    g10: LineSegment StartX=-4.25 StartY=-5.8823 StartZ=0 EndX=0 EndY=0 EndZ=0
    g11: LineSegment StartX=-4.25 StartY=5.8823 StartZ=0 EndX=4.25 EndY=5.8823 EndZ=0
    g12: LineSegment StartX=-4.25 StartY=-5.8823 StartZ=0 EndX=4.25 EndY=-5.8823 EndZ=0
  constraints (33):
    c: Coincident(g0,g1)
    c: Coincident(g1,g2)
    c: Coincident(g2,g3)
    c: Coincident(g3,g0)
    c: Horizontal(g0)
    c: Horizontal(g2)
    c: Vertical(g1)
    c: Vertical(g3)
    c: Coincident(g4,g5)
    c: Coincident(g5,g6)
    c: Coincident(g6,g7)
    c: Coincident(g7,g4)
    c: Horizontal(g4)
    c: Horizontal(g6)
    c: Vertical(g5)
    c: Vertical(g7)
    c: Coincident(g0,g8)
    c: Coincident(g8,g-1)
    c: Coincident(g8,g9)
    c: Coincident(g9,g4)
    c: Coincident(g1,g10)
    c: Coincident(g10,g-1)
    c: Equal(g10,g8)
    c: Equal(g8,g9)
    c: Equal(g5,g1)
    c: Equal(g0,g4)
    c: Coincident(g11,g0)
    c: Coincident(g11,g4)
    c: Coincident(g12,g1)
    c: Coincident(g12,g5)
    c: Horizontal(g12)
    c: DistanceX(g0,g0) = 2
    c: DistanceX(g11,g11) = 8.5
FEATURE [PartDesign::Pocket] Pocket006
  BaseFeature = -> Revolution002
  Direction = (1,1,1)
  Length = 5
  Length2 = 100
  Midplane = true
  Placement = pos=(0,0,0) rot=(0.57735,0.57735,0.57735;2.0944rad)
  Profile = -> Sketch021
  Type = 1
FEATURE [PartDesign::Body] Body066  label="Bushing001"
  Group = -> [Sketch020,Revolution002,Sketch021,Pocket006]
  Origin = -> Origin070
  Tip = -> Pocket006
FEATURE [PartDesign::FeatureBase] Clone061
  BaseFeature = -> Body066
FEATURE [PartDesign::Body] Body068
  BaseFeature = -> Body066
  Group = -> [Clone061]
  Origin = -> Origin073
  Placement = pos=(0,12,0) rot=(0,0,1;0rad)
  Tip = -> Clone061
FEATURE [PartDesign::FeatureBase] Clone063
  BaseFeature = -> Body066
FEATURE [PartDesign::Body] Body070
  BaseFeature = -> Body066
  Group = -> [Clone063]
  Origin = -> Origin075
  Placement = pos=(0,24,0) rot=(0,0,1;0rad)
  Tip = -> Clone063
FEATURE [PartDesign::FeatureBase] Clone065
  BaseFeature = -> Body066
FEATURE [PartDesign::Body] Body072
  BaseFeature = -> Body066
  Group = -> [Clone065]
  Origin = -> Origin077
  Placement = pos=(0,36,0) rot=(0,0,1;0rad)
  Tip = -> Clone065
FEATURE [PartDesign::FeatureBase] Clone067
  BaseFeature = -> Body066
FEATURE [PartDesign::Body] Body074
  BaseFeature = -> Body066
  Group = -> [Clone067]
  Origin = -> Origin079
  Placement = pos=(0,48,0) rot=(0,0,1;0rad)
  Tip = -> Clone067
FEATURE [PartDesign::FeatureBase] Clone069
  BaseFeature = -> Body066
FEATURE [PartDesign::Body] Body076
  BaseFeature = -> Body066
  Group = -> [Clone069]
  Origin = -> Origin081
  Placement = pos=(0,60,0) rot=(0,0,1;0rad)
  Tip = -> Clone069
FEATURE [PartDesign::FeatureBase] Clone071
  BaseFeature = -> Body066
FEATURE [PartDesign::Body] Body078
  BaseFeature = -> Body066
  Group = -> [Clone071]
  Origin = -> Origin083
  Placement = pos=(0,72,0) rot=(0,0,1;0rad)
  Tip = -> Clone071
FEATURE [PartDesign::FeatureBase] Clone072
  BaseFeature = -> Body066
FEATURE [PartDesign::Body] Body079
  BaseFeature = -> Body066
  Group = -> [Clone072]
  Origin = -> Origin084
  Placement = pos=(0,84,0) rot=(0,0,1;0rad)
  Tip = -> Clone072
FEATURE [App::Part] Part004  label="Bushing"
  Group = -> [Body066,Body068,Body070,Body072,Body074,Body076,Body078,Body079]
  Origin = -> Origin071
FEATURE [Sketcher::SketchObject] Sketch022
  FullyConstrained = true
  MapMode = 5
  Support = -> [XY_Plane085]
  sketch-geometry (2):
    g0: ArcOfCircle CenterX=0 CenterY=0 CenterZ=0 NormalX=0 NormalY=0 NormalZ=1 AngleXU=0 Radius=2.95 StartAngle=5.55407 EndAngle=10.1539
    g1: LineSegment StartX=-2.2 StartY=-1.96532 StartZ=0 EndX=2.2 EndY=-1.96532 EndZ=0
  constraints (6):
    c: Coincident(g0,g-1)
    c: Coincident(g1,g0)
    c: Coincident(g1,g0)
    c: Radius(g0) = 2.95
    c: DistanceX(g1,g1) = 4.4
    c: Horizontal(g1)
FEATURE [PartDesign::Pad] Pad008  label="Riser004"
  AllowMultiFace = false
  Direction = (0,0,1)
  Length = 6.5
  Length2 = 100
  Profile = -> Sketch022
  Refine = true
  Type = 0
FEATURE [Sketcher::SketchObject] Sketch024
  FullyConstrained = true
  MapMode = 5
  Placement = pos=(0,0,0) rot=(0.57735,0.57735,0.57735;2.0944rad)
  Support = -> [YZ_Plane085]
  sketch-geometry (6):
    g0: LineSegment StartX=-1.97 StartY=6.5 StartZ=0 EndX=-1.67 EndY=5.5 EndZ=0
    g1: LineSegment StartX=-1.67 StartY=5.5 StartZ=0 EndX=-1.67 EndY=2.4 EndZ=0
    g2: LineSegment StartX=-1.67 StartY=2.4 StartZ=0 EndX=-1.22 EndY=1.4 EndZ=0
    g3: LineSegment StartX=-1.22 StartY=1.4 StartZ=0 EndX=4 EndY=1.4 EndZ=0
    g4: LineSegment StartX=4 StartY=1.4 StartZ=0 EndX=4 EndY=6.5 EndZ=0
    g5: LineSegment StartX=4 StartY=6.5 StartZ=0 EndX=-1.97 EndY=6.5 EndZ=0
  constraints (18):
    c: Coincident(g0,g1)
    c: Vertical(g1)
    c: Coincident(g1,g2)
    c: Coincident(g2,g3)
    c: Horizontal(g3)
    c: Coincident(g3,g4)
    c: Vertical(g4)
    c: Coincident(g4,g5)
    c: Coincident(g5,g0)
    c: Horizontal(g5)
    c: DistanceX(g0,g-1) = 1.97
    c: DistanceY(g-1,g0) = 6.5
    c: DistanceX(g0,g0) = 0.3
    c: DistanceY(g0,g0) = 1
    c: DistanceY(g2,g2) = 1
    c: DistanceX(g2,g2) = 0.45
    c: DistanceX(g-1,g3) = 4
    c: DistanceY(g-1,g3) = 1.4
FEATURE [PartDesign::Pocket] Pocket007
  BaseFeature = -> Pad008
  Direction = (-1,2e-16,-3e-16)
  Length = 5
  Length2 = 100
  Midplane = true
  Profile = -> Sketch024
  Type = 1
FEATURE [Sketcher::SketchObject] Sketch023
  FullyConstrained = true
  MapMode = 5
  Placement = pos=(-4e-16,3e-16,1.4) rot=(0,0,1;0rad)
  Support = -> [Pocket007]
  sketch-geometry (1):
    g0: Circle CenterX=0 CenterY=0.5 CenterZ=0 NormalX=0 NormalY=0 NormalZ=1 AngleXU=0 Radius=0.8
  constraints (3):
    c: PointOnObject(g0,g-2)
    c: DistanceY(g-1,g0) = 0.5
    c: Diameter(g0) = 1.6
FEATURE [PartDesign::Pad] Pad009
  BaseFeature = -> Pocket007
  Direction = (-3e-16,2e-16,1)
  Length = 0.4
  Length2 = 100
  Profile = -> Sketch023
  ReferenceAxis = -> Sketch023 [N_Axis]
  Type = 0
FEATURE [PartDesign::Fillet] Fillet001
  Base = -> Pad009 [Edge18]
  BaseFeature = -> Pad009
  Radius = 0.3
  SupportTransform = false
  UseAllEdges = false
FEATURE [PartDesign::Chamfer] Chamfer007
  Angle = 45
  Base = -> Fillet001 [Face7]
  BaseFeature = -> Fillet001
  ChamferType = 0
  FlipDirection = false
  Size = 0.4
  Size2 = 1
  SupportTransform = false
  UseAllEdges = false
FEATURE [PartDesign::Body] Body080  label="Encoder_new"
  Group = -> [Sketch022,Pad008,Sketch023,Sketch024,Pocket007,Pad009,Fillet001,Chamfer007]
  Origin = -> Origin085
  Tip = -> Chamfer007
FEATURE [PartDesign::FeatureBase] Clone073
  BaseFeature = -> Body080
FEATURE [PartDesign::Body] Body081
  BaseFeature = -> Body080
  Group = -> [Clone073]
  Origin = -> Origin087
  Placement = pos=(0,6,0) rot=(0,0,1;0rad)
  Tip = -> Clone073
FEATURE [PartDesign::FeatureBase] Clone074
  BaseFeature = -> Body080
FEATURE [PartDesign::Body] Body082
  BaseFeature = -> Body080
  Group = -> [Clone074]
  Origin = -> Origin088
  Placement = pos=(0,12,0) rot=(0,0,1;0rad)
  Tip = -> Clone074
FEATURE [PartDesign::FeatureBase] Clone075
  BaseFeature = -> Body080
FEATURE [PartDesign::Body] Body083
  BaseFeature = -> Body080
  Group = -> [Clone075]
  Origin = -> Origin089
  Placement = pos=(0,18,0) rot=(0,0,1;0rad)
  Tip = -> Clone075
FEATURE [PartDesign::FeatureBase] Clone076
  BaseFeature = -> Body080
FEATURE [PartDesign::Body] Body084
  BaseFeature = -> Body080
  Group = -> [Clone076]
  Origin = -> Origin090
  Placement = pos=(0,24,0) rot=(0,0,1;0rad)
  Tip = -> Clone076
FEATURE [PartDesign::FeatureBase] Clone077
  BaseFeature = -> Body080
FEATURE [PartDesign::Body] Body085
  BaseFeature = -> Body080
  Group = -> [Clone077]
  Origin = -> Origin091
  Placement = pos=(0,30,0) rot=(0,0,1;0rad)
  Tip = -> Clone077
FEATURE [PartDesign::FeatureBase] Clone078
  BaseFeature = -> Body080
FEATURE [PartDesign::Body] Body086
  BaseFeature = -> Body080
  Group = -> [Clone078]
  Origin = -> Origin092
  Placement = pos=(0,36,0) rot=(0,0,1;0rad)
  Tip = -> Clone078
FEATURE [PartDesign::FeatureBase] Clone079
  BaseFeature = -> Body080
FEATURE [PartDesign::Body] Body087
  BaseFeature = -> Body080
  Group = -> [Clone079]
  Origin = -> Origin093
  Placement = pos=(0,42,0) rot=(0,0,1;0rad)
  Tip = -> Clone079
FEATURE [PartDesign::FeatureBase] Clone080
  BaseFeature = -> Body080
FEATURE [PartDesign::Body] Body088
  BaseFeature = -> Body080
  Group = -> [Clone080]
  Origin = -> Origin094
  Placement = pos=(0,48,0) rot=(0,0,1;0rad)
  Tip = -> Clone080
FEATURE [PartDesign::FeatureBase] Clone081
  BaseFeature = -> Body080
FEATURE [PartDesign::Body] Body089
  BaseFeature = -> Body080
  Group = -> [Clone081]
  Origin = -> Origin095
  Placement = pos=(0,54,0) rot=(0,0,1;0rad)
  Tip = -> Clone081
FEATURE [PartDesign::FeatureBase] Clone082
  BaseFeature = -> Body080
FEATURE [PartDesign::Body] Body090
  BaseFeature = -> Body080
  Group = -> [Clone082]
  Origin = -> Origin096
  Placement = pos=(0,60,0) rot=(0,0,1;0rad)
  Tip = -> Clone082
FEATURE [PartDesign::FeatureBase] Clone083
  BaseFeature = -> Body080
FEATURE [PartDesign::Body] Body091
  BaseFeature = -> Body080
  Group = -> [Clone083]
  Origin = -> Origin097
  Placement = pos=(0,66,0) rot=(0,0,1;0rad)
  Tip = -> Clone083
FEATURE [PartDesign::FeatureBase] Clone084
  BaseFeature = -> Body080
FEATURE [PartDesign::Body] Body092
  BaseFeature = -> Body080
  Group = -> [Clone084]
  Origin = -> Origin098
  Placement = pos=(0,72,0) rot=(0,0,1;0rad)
  Tip = -> Clone084
FEATURE [PartDesign::FeatureBase] Clone085
  BaseFeature = -> Body080
FEATURE [PartDesign::Body] Body093
  BaseFeature = -> Body080
  Group = -> [Clone085]
  Origin = -> Origin099
  Placement = pos=(0,78,0) rot=(0,0,1;0rad)
  Tip = -> Clone085
FEATURE [PartDesign::FeatureBase] Clone086
  BaseFeature = -> Body080
FEATURE [PartDesign::Body] Body094
  BaseFeature = -> Body080
  Group = -> [Clone086]
  Origin = -> Origin100
  Placement = pos=(0,84,0) rot=(0,0,1;0rad)
  Tip = -> Clone086
FEATURE [PartDesign::FeatureBase] Clone087
  BaseFeature = -> Body080
FEATURE [PartDesign::Body] Body095
  BaseFeature = -> Body080
  Group = -> [Clone087]
  Origin = -> Origin101
  Placement = pos=(0,90,0) rot=(0,0,1;0rad)
  Tip = -> Clone087
FEATURE [App::Part] Part005  label="E_new"
  Group = -> [Body080,Body081,Body082,Body083,Body084,Body085,Body086,Body087,Body088,Body089,Body090,Body091,Body092,Body093,Body094,Body095]
  Origin = -> Origin086
FEATURE [PartDesign::Chamfer] Chamfer008
  Angle = 45
  Base = -> Pocket005 [Face2]
  BaseFeature = -> Pocket005
  ChamferType = 0
  FlipDirection = false
  Size = 0.6
  Size2 = 1
  SupportTransform = false
  UseAllEdges = false
FEATURE [PartDesign::Body] Body050  label="Potentiometer001"
  Group = -> [Sketch018,Pad007,Sketch019,Pocket005,Chamfer008]
  Origin = -> Origin053
  Tip = -> Chamfer008
FEATURE [PartDesign::FeatureBase] Clone045
  BaseFeature = -> Body050
FEATURE [PartDesign::Body] Body051
  BaseFeature = -> Body050
  Group = -> [Clone045]
  Origin = -> Origin055
  Placement = pos=(0,6,0) rot=(0,0,1;0rad)
  Tip = -> Clone045
FEATURE [PartDesign::FeatureBase] Clone046
  BaseFeature = -> Body050
FEATURE [PartDesign::Body] Body052
  BaseFeature = -> Body050
  Group = -> [Clone046]
  Origin = -> Origin056
  Placement = pos=(0,12,0) rot=(0,0,1;0rad)
  Tip = -> Clone046
FEATURE [PartDesign::FeatureBase] Clone047
  BaseFeature = -> Body050
FEATURE [PartDesign::Body] Body053
  BaseFeature = -> Body050
  Group = -> [Clone047]
  Origin = -> Origin057
  Placement = pos=(0,18,0) rot=(0,0,1;0rad)
  Tip = -> Clone047
FEATURE [PartDesign::FeatureBase] Clone048
  BaseFeature = -> Body050
FEATURE [PartDesign::Body] Body054
  BaseFeature = -> Body050
  Group = -> [Clone048]
  Origin = -> Origin058
  Placement = pos=(0,24,0) rot=(0,0,1;0rad)
  Tip = -> Clone048
FEATURE [PartDesign::FeatureBase] Clone049
  BaseFeature = -> Body050
FEATURE [PartDesign::Body] Body055
  BaseFeature = -> Body050
  Group = -> [Clone049]
  Origin = -> Origin059
  Placement = pos=(0,30,0) rot=(0,0,1;0rad)
  Tip = -> Clone049
FEATURE [PartDesign::FeatureBase] Clone050
  BaseFeature = -> Body050
FEATURE [PartDesign::Body] Body056
  BaseFeature = -> Body050
  Group = -> [Clone050]
  Origin = -> Origin060
  Placement = pos=(0,36,0) rot=(0,0,1;0rad)
  Tip = -> Clone050
FEATURE [PartDesign::FeatureBase] Clone051
  BaseFeature = -> Body050
FEATURE [PartDesign::Body] Body057
  BaseFeature = -> Body050
  Group = -> [Clone051]
  Origin = -> Origin061
  Placement = pos=(0,42,0) rot=(0,0,1;0rad)
  Tip = -> Clone051
FEATURE [PartDesign::FeatureBase] Clone052
  BaseFeature = -> Body050
FEATURE [PartDesign::Body] Body058
  BaseFeature = -> Body050
  Group = -> [Clone052]
  Origin = -> Origin062
  Placement = pos=(0,48,0) rot=(0,0,1;0rad)
  Tip = -> Clone052
FEATURE [PartDesign::FeatureBase] Clone053
  BaseFeature = -> Body050
FEATURE [PartDesign::Body] Body059
  BaseFeature = -> Body050
  Group = -> [Clone053]
  Origin = -> Origin063
  Placement = pos=(0,54,0) rot=(0,0,1;0rad)
  Tip = -> Clone053
FEATURE [PartDesign::FeatureBase] Clone054
  BaseFeature = -> Body050
FEATURE [PartDesign::Body] Body060
  BaseFeature = -> Body050
  Group = -> [Clone054]
  Origin = -> Origin064
  Placement = pos=(0,60,0) rot=(0,0,1;0rad)
  Tip = -> Clone054
FEATURE [PartDesign::FeatureBase] Clone055
  BaseFeature = -> Body050
FEATURE [PartDesign::Body] Body061
  BaseFeature = -> Body050
  Group = -> [Clone055]
  Origin = -> Origin065
  Placement = pos=(0,66,0) rot=(0,0,1;0rad)
  Tip = -> Clone055
FEATURE [PartDesign::FeatureBase] Clone056
  BaseFeature = -> Body050
FEATURE [PartDesign::Body] Body062
  BaseFeature = -> Body050
  Group = -> [Clone056]
  Origin = -> Origin066
  Placement = pos=(0,72,0) rot=(0,0,1;0rad)
  Tip = -> Clone056
FEATURE [PartDesign::FeatureBase] Clone057
  BaseFeature = -> Body050
FEATURE [PartDesign::Body] Body063
  BaseFeature = -> Body050
  Group = -> [Clone057]
  Origin = -> Origin067
  Placement = pos=(0,78,0) rot=(0,0,1;0rad)
  Tip = -> Clone057
FEATURE [PartDesign::FeatureBase] Clone058
  BaseFeature = -> Body063
FEATURE [PartDesign::Body] Body064
  BaseFeature = -> Body063
  Group = -> [Clone058]
  Origin = -> Origin068
  Placement = pos=(0,84,0) rot=(0,0,1;0rad)
  Tip = -> Clone058
FEATURE [PartDesign::FeatureBase] Clone059
  BaseFeature = -> Body063
FEATURE [PartDesign::Body] Body065
  BaseFeature = -> Body063
  Group = -> [Clone059]
  Origin = -> Origin069
  Placement = pos=(0,90,0) rot=(0,0,1;0rad)
  Tip = -> Clone059
FEATURE [App::Part] Part003  label="P_new"
  Group = -> [Body050,Body051,Body052,Body053,Body054,Body055,Body056,Body057,Body058,Body059,Body060,Body061,Body062,Body063,Body064,Body065]
  Origin = -> Origin054
